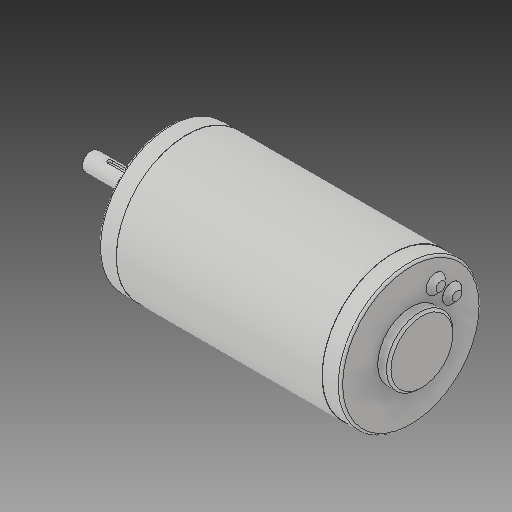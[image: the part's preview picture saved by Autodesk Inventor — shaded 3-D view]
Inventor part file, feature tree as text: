
AUTODESK INVENTOR PART (.ipt)
format: ipt  version: 2017 (Build 210142000, 142)  size: 155,136 bytes
history: native  units: in
note: dims shown in document units (in); Inventor stores cm internally (conversion verified against a paired STEP export)
features: chamfer x1
ambient origin geometry x8: Origin, YZ Plane, XZ Plane, XY Plane, X Axis, Y Axis, Z Axis, Center Point
bodies: Solid1 (feature_tree)
feature tree (1):
  chamfer  "Chamfer3"  [1 undecoded]
note: 1 required parameter value undecoded (feature->parameter linkage not recoverable at this tier; creation-order binding heuristic only, values carry confidence <= 0.55)
